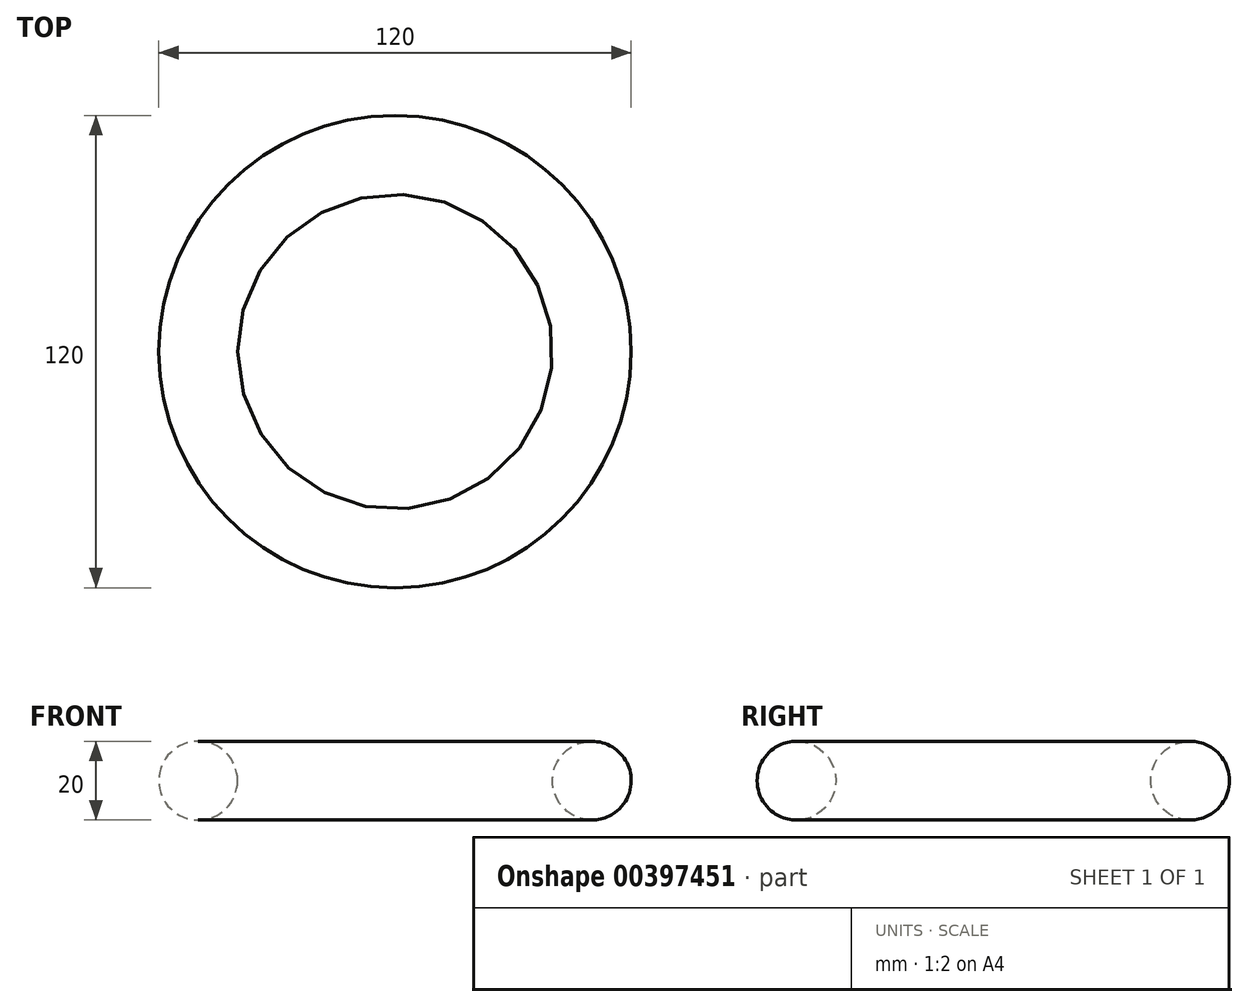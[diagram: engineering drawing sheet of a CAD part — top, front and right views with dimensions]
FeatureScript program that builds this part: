
annotation { "Feature Type Name" : "Feature", "Feature Type Description" : "" }
export const myFeature = defineFeature(function(context is Context, id is Id, definition is map)
    precondition{}
    {
        {
            var Q0;
            Q0=qCreatedBy(makeId("Top.planeOp"),FACE);
            var sketch = newSketch(context, id + "F0", { "sketchPlane" : qUnion([Q0])});
            skCircle(sketch, "E0", {"center": v(0, 0) * mm, "radius": 50 * mm});
            skSolve(sketch);
        }
        {
            var Q0;
            Q0=qCreatedBy(makeId("Front.planeOp"),FACE);
            var sketch = newSketch(context, id + "F1", { "sketchPlane" : qUnion([Q0])});
            skCircle(sketch, "E1", {"center": v(-50, 0) * mm, "radius": 10 * mm});
            skSolve(sketch);
        }
        {
            var Q0;
            Q0=makeQuery(id+"F1.imprint","IMPRINT",FACE,{"disambiguationData":[TD([[makeQuery(id+"F1.imprint","IMPRINT",EDGE,{"derivedFrom":sQuery(id+"F1.wireOp",EDGE,"E1")}),1.0]])]});
            var Q1;
            Q1=sQuery(id+"F0.wireOp",EDGE,"E0");
            revolve(context, id + "F2", {"entities" : qUnion([Q0]), "axis" : qUnion([Q1]), "revolveType" : RevolveType.FULL});
        }
    });
